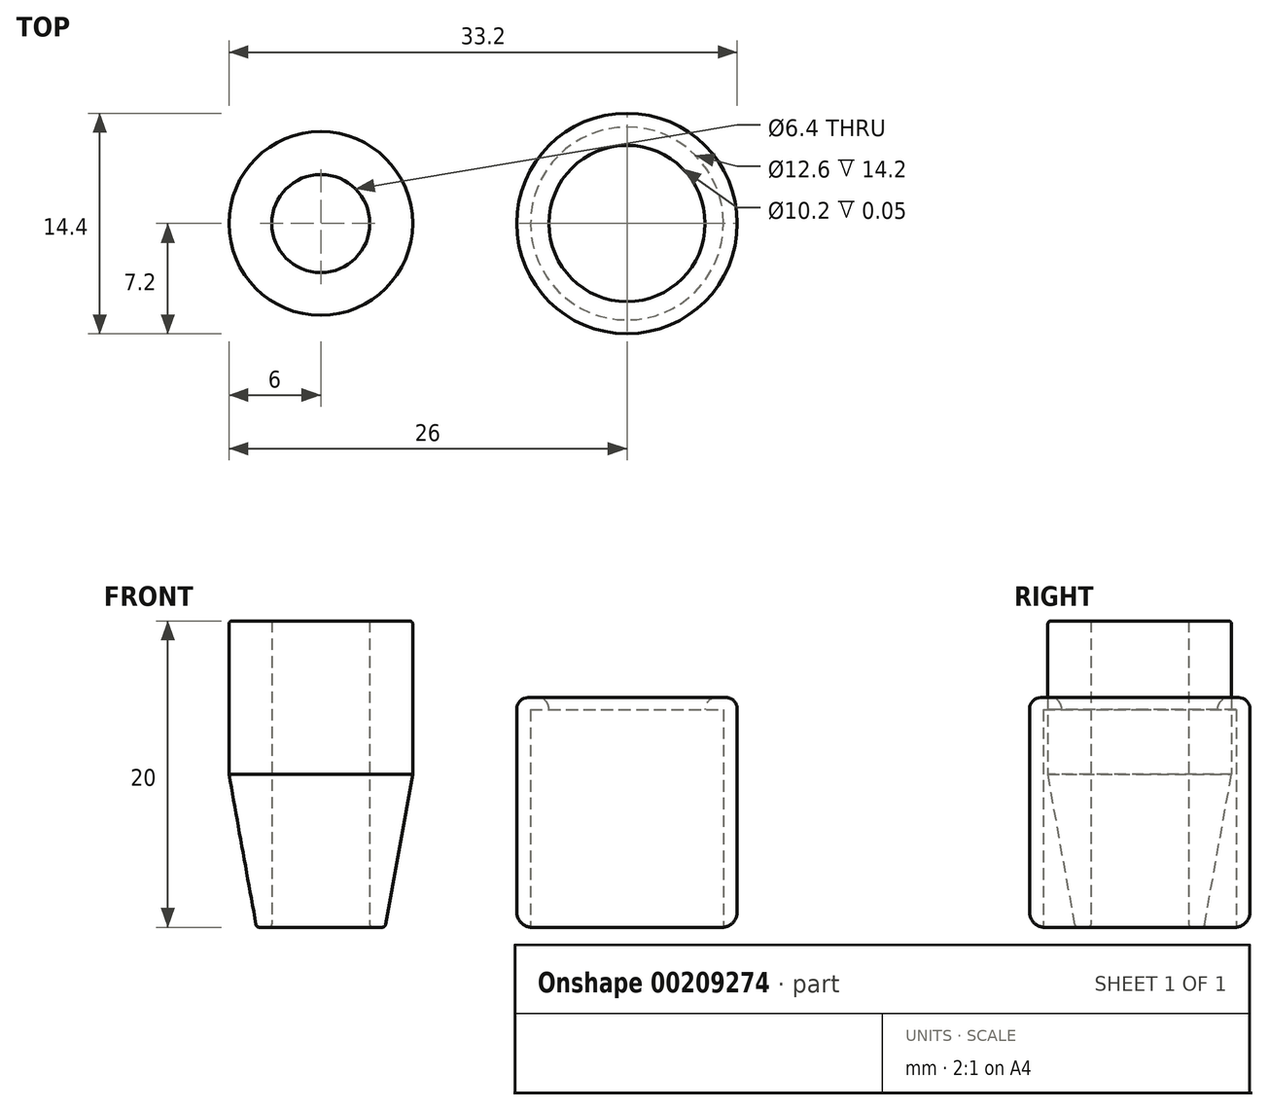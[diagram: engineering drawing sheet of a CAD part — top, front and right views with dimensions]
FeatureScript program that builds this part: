
annotation { "Feature Type Name" : "Feature", "Feature Type Description" : "" }
export const myFeature = defineFeature(function(context is Context, id is Id, definition is map)
    precondition{}
    {
        {
            var Q0;
            Q0=qCreatedBy(makeId("Front.planeOp"),FACE);
            var sketch = newSketch(context, id + "F0", { "sketchPlane" : qUnion([Q0])});
            skLineSegment(sketch, "E0", {"start": v(0, 8) * mm, "end": v(-3.2, 8) * mm});
            skLineSegment(sketch, "E1", {"start": v(-3.2, 0) * mm, "end": v(-7.2, 0) * mm});
            skLineSegment(sketch, "E2", {"start": v(-7.2, 0) * mm, "end": v(-7.2, 15) * mm});
            skLineSegment(sketch, "E3", {"start": v(-7.2, 15) * mm, "end": v(-5.1, 15) * mm});
            skLineSegment(sketch, "E4.right", {"start": v(-6.3, 8) * mm, "end": v(-6.3, 14.2) * mm});
            skLineSegment(sketch, "E5", {"start": v(-5.1, 15) * mm, "end": v(-5.1, 14.2) * mm});
            skLineSegment(sketch, "E6", {"start": v(-5.1, 14.2) * mm, "end": v(-6.3, 14.2) * mm});
            skLineSegment(sketch, "E7", {"start": v(0, 0) * mm, "end": v(0, 8) * mm});
            skLineSegment(sketch, "E8", {"start": v(-6.3, 8) * mm, "end": v(0, 8) * mm});
            skLineSegment(sketch, "E9", {"start": v(-6.3, 8) * mm, "end": v(-7.2, 8) * mm});
            skLineSegment(sketch, "E10", {"start": v(-6.3, 8) * mm, "end": v(-6.3, 0) * mm});
            skLineSegment(sketch, "E11", {"start": v(0, 27.23) * mm, "end": v(0, 17.23) * mm, "construction": true});
            skLineSegment(sketch, "E12", {"start": v(-3.2, 17.23) * mm, "end": v(-3.2, 27.23) * mm});
            skLineSegment(sketch, "E13", {"start": v(-3.2, 17.23) * mm, "end": v(-4.2, 17.23) * mm});
            skLineSegment(sketch, "E14", {"start": v(-4.2, 17.23) * mm, "end": v(-6, 27.23) * mm});
            skLineSegment(sketch, "E15.bottom", {"start": v(-3.2, 27.23) * mm, "end": v(-6, 27.23) * mm});
            skLineSegment(sketch, "E15.top", {"start": v(-3.2, 37.23) * mm, "end": v(-6, 37.23) * mm});
            skLineSegment(sketch, "E15.left", {"start": v(-3.2, 27.23) * mm, "end": v(-3.2, 37.23) * mm});
            skLineSegment(sketch, "E15.right", {"start": v(-6, 27.23) * mm, "end": v(-6, 37.23) * mm});
            skLineSegment(sketch, "E16", {"start": v(0, 27.23) * mm, "end": v(-3.2, 27.23) * mm, "construction": true});
            skSolve(sketch);
        }
        {
            var Q0;
            Q0=qSketchRegion(id+"F0",true);
            var Q1;
            Q1=sQuery(id+"F0.wireOp",EDGE,"E7");
            revolve(context, id + "F1", {"entities" : qUnion([Q0]), "axis" : qUnion([Q1]), "revolveType" : RevolveType.FULL});
        }
        {
            var Q0;
            Q0=makeQuery(id+"F1.opRevolve","SWEPT_FACE",FACE,{"disambiguationData":[OSD([sQuery(id+"F0.wireOp",EDGE,"E3")])]});
            fillet(context, id + "F2", {"entities" : qUnion([Q0]), "radius" : 0.75 * mm, "tangentPropagation" : true, "allowEdgeOverflow" : false});
        }
        {
            var Q0;
            Q0=makeQuery(id+"F1.opRevolve","SWEPT_EDGE",EDGE,{"disambiguationData":[OSD([sQuery(id+"F0.wireOp",EDGE,"E1"),sQuery(id+"F0.wireOp",EDGE,"E2")])]});
            fillet(context, id + "F3", {"entities" : qUnion([Q0]), "radius" : 1 * mm, "tangentPropagation" : true, "allowEdgeOverflow" : false});
        }
        {
            var Q0;
            Q0=makeQuery(id+"F1.opRevolve","SWEPT_EDGE",EDGE,{"disambiguationData":[OSD([sQuery(id+"F0.wireOp",EDGE,"E15.top"),sQuery(id+"F0.wireOp",EDGE,"E15.right")])]});
            var Q1;
            Q1=makeQuery(id+"F1.opRevolve","SWEPT_EDGE",EDGE,{"disambiguationData":[OSD([sQuery(id+"F0.wireOp",EDGE,"E12"),sQuery(id+"F0.wireOp",EDGE,"E13")])]});
            var Q2;
            Q2=makeQuery(id+"F1.opRevolve","SWEPT_EDGE",EDGE,{"disambiguationData":[OSD([sQuery(id+"F0.wireOp",EDGE,"E13"),sQuery(id+"F0.wireOp",EDGE,"E14")])]});
            fillet(context, id + "F4", {"entities" : qUnion([Q0, Q1, Q2]), "radius" : 0.2 * mm, "tangentPropagation" : true, "allowEdgeOverflow" : false});
        }
        {
            var Q0;
            Q0=makeQuery(id+"F1.opRevolve","SWEPT_BODY",BODY,{"disambiguationData":[OSD([sQuery(id+"F0.wireOp",EDGE,"E1"),sQuery(id+"F0.wireOp",EDGE,"E2"),sQuery(id+"F0.wireOp",EDGE,"E3"),sQuery(id+"F0.wireOp",EDGE,"E4.right"),sQuery(id+"F0.wireOp",EDGE,"E5"),sQuery(id+"F0.wireOp",EDGE,"E6"),sQuery(id+"F0.wireOp",EDGE,"E10")])]});
            transform(context, id + "F5", {"entities" : qUnion([Q0]), "transformType" : TransformType.TRANSLATION_3D, "dx" : 10 * mm, "dy" : 0 * mm, "dz" : 0 * mm, "makeCopy" : true});
        }
        {
            var Q0;
            Q0=makeQuery(id+"F1.opRevolve","SWEPT_BODY",BODY,{"disambiguationData":[OSD([sQuery(id+"F0.wireOp",EDGE,"E1"),sQuery(id+"F0.wireOp",EDGE,"E2"),sQuery(id+"F0.wireOp",EDGE,"E3"),sQuery(id+"F0.wireOp",EDGE,"E4.right"),sQuery(id+"F0.wireOp",EDGE,"E5"),sQuery(id+"F0.wireOp",EDGE,"E6"),sQuery(id+"F0.wireOp",EDGE,"E10")])]});
            deleteBodies(context, id + "F6", {"entities" : qUnion([Q0])});
        }
        {
            var Q0;
            Q0=makeQuery(id+"F1.opRevolve","SWEPT_BODY",BODY,{"disambiguationData":[OSD([sQuery(id+"F0.wireOp",EDGE,"E12"),sQuery(id+"F0.wireOp",EDGE,"E13"),sQuery(id+"F0.wireOp",EDGE,"E14"),sQuery(id+"F0.wireOp",EDGE,"E15.top"),sQuery(id+"F0.wireOp",EDGE,"E15.left"),sQuery(id+"F0.wireOp",EDGE,"E15.right")])]});
            transform(context, id + "F7", {"entities" : qUnion([Q0]), "transformType" : TransformType.TRANSLATION_3D, "dx" : -10 * mm, "dy" : 0 * mm, "dz" : -17.23 * mm, "makeCopy" : true});
        }
        {
            var Q0;
            Q0=makeQuery(id+"F1.opRevolve","SWEPT_BODY",BODY,{"disambiguationData":[OSD([sQuery(id+"F0.wireOp",EDGE,"E12"),sQuery(id+"F0.wireOp",EDGE,"E13"),sQuery(id+"F0.wireOp",EDGE,"E14"),sQuery(id+"F0.wireOp",EDGE,"E15.top"),sQuery(id+"F0.wireOp",EDGE,"E15.left"),sQuery(id+"F0.wireOp",EDGE,"E15.right")])]});
            deleteBodies(context, id + "F8", {"entities" : qUnion([Q0])});
        }
    });
